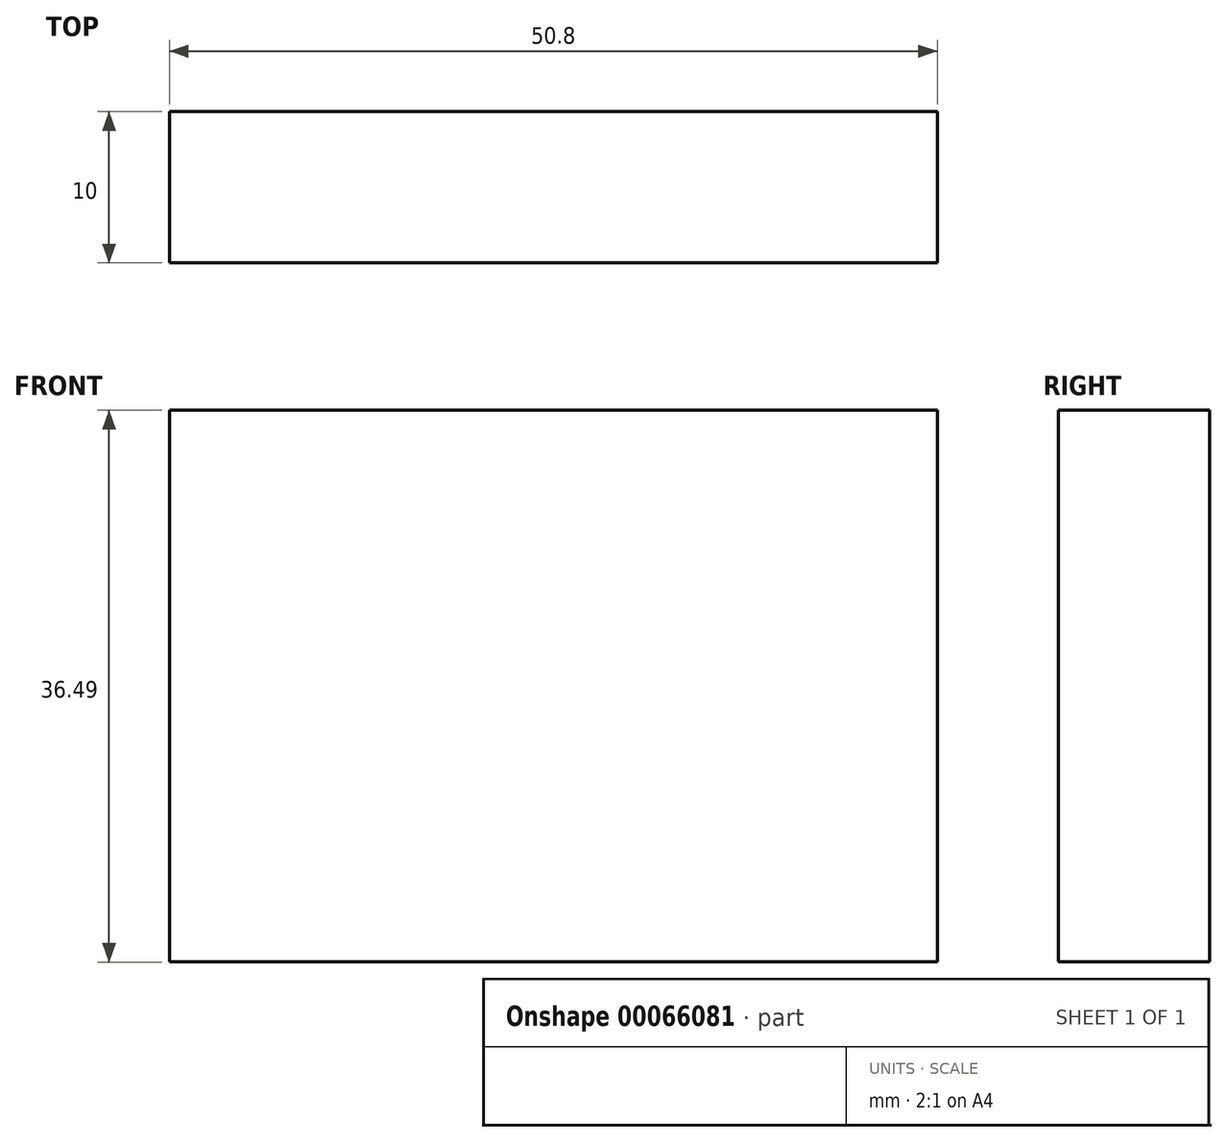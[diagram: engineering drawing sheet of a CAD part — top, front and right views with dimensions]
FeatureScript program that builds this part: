
annotation { "Feature Type Name" : "Feature", "Feature Type Description" : "" }
export const myFeature = defineFeature(function(context is Context, id is Id, definition is map)
    precondition{}
    {
        {
            var Q0;
            Q0=qCreatedBy(makeId("Front.planeOp"),FACE);
            var sketch = newSketch(context, id + "F0", { "sketchPlane" : qUnion([Q0])});
            skLineSegment(sketch, "E0.rect.bottom", {"start": v(33.15, -6.5) * mm, "end": v(-17.65, -6.5) * mm});
            skLineSegment(sketch, "E0.rect.top", {"start": v(33.15, 29.98) * mm, "end": v(-17.65, 29.98) * mm});
            skPoint(sketch, "E1.rect.middle", {"position": v(7.75, -14.93) * mm});
            skLineSegment(sketch, "E0.rect.left", {"start": v(33.15, -6.5) * mm, "end": v(33.15, 29.98) * mm});
            skLineSegment(sketch, "E0.rect.right", {"start": v(-17.65, -6.5) * mm, "end": v(-17.65, 29.98) * mm});
            skPoint(sketch, "E0.rect.middle", {"position": v(7.75, 11.74) * mm});
            skSolve(sketch);
        }
        {
            var Q0;
            Q0=makeQuery(id+"F0.imprint","IMPRINT",FACE,{"disambiguationData":[TD([[makeQuery(id+"F0.imprint","IMPRINT",EDGE,{"derivedFrom":sQuery(id+"F0.wireOp",EDGE,"E0.rect.bottom")}),-1.0]])]});
            extrude(context, id + "F1", {"entities" : qUnion([Q0]), "depth" : 10 * mm});
        }
    });
